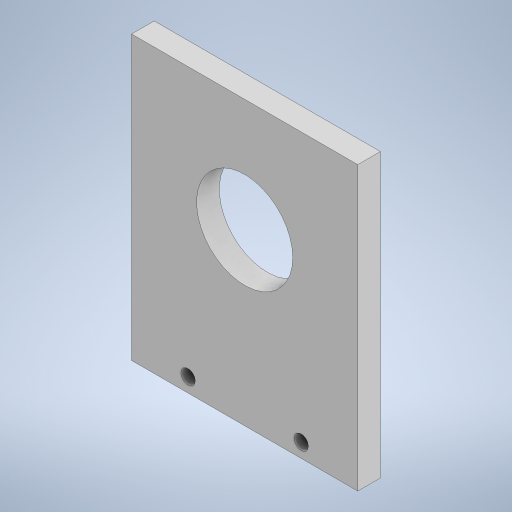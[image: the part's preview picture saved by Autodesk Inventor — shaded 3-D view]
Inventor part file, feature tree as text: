
AUTODESK INVENTOR PART (.ipt)
format: ipt  version: 2024 (Build 280153000, 153)  size: 233,472 bytes
history: native  units: in
note: dims shown in document units (in); Inventor stores cm internally (conversion verified against a paired STEP export)
features: extrude x3, sketch x3
ambient origin geometry x8: Origin, YZ Plane, XZ Plane, XY Plane, X Axis, Y Axis, Z Axis, Center Point
bodies: Solid1 (feature_tree)
feature tree (6):
  extrude  "Extrusion1"  Depth=9.8425in
  extrude  "Extrusion2"  Depth=0.7874in
  extrude  "Extrusion3"  Depth=0.7874in
  sketch  "Sketch1"  dims[d0=7.874in d1=9.8425in]
  sketch  "Sketch2"  dims[d2=0.7874in d3=0.0in d4=3.3465in]
  sketch  "Sketch3"  dims[d5=3.937in d6=3.937in d7=0.7874in d8=0.0in d9=0.5in d10=0.5in d11=0.4921in d12=0.4921in d13=1.9685in d14=1.9685in d15=0.7874in d16=0.0in]
